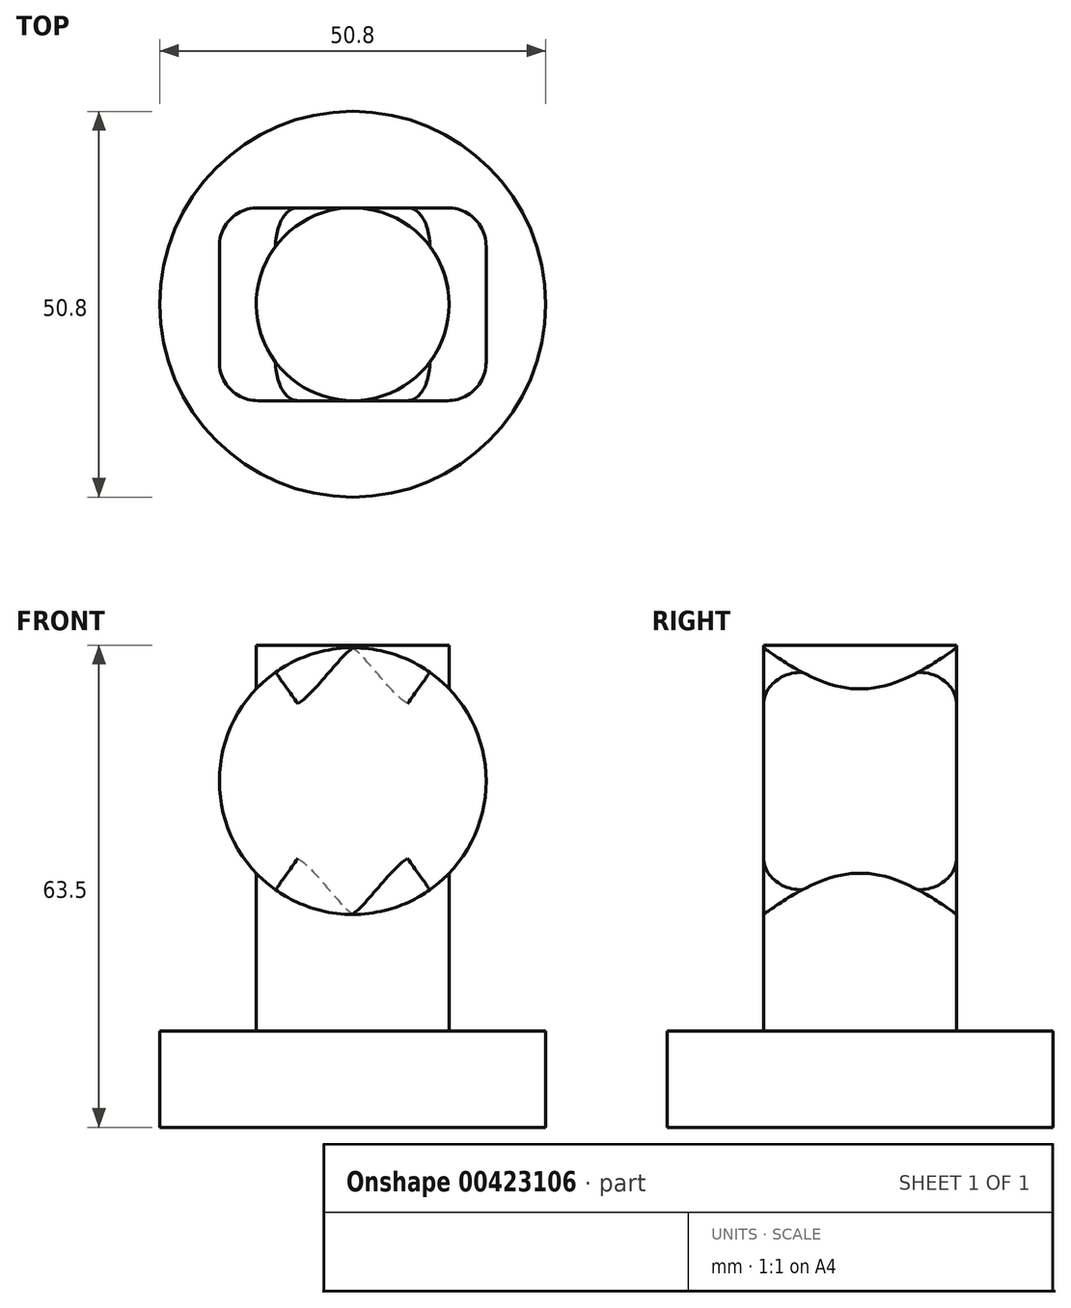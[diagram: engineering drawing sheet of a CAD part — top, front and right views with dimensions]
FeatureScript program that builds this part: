
annotation { "Feature Type Name" : "Feature", "Feature Type Description" : "" }
export const myFeature = defineFeature(function(context is Context, id is Id, definition is map)
    precondition{}
    {
        {
            var Q0;
            Q0=qCreatedBy(makeId("Top.planeOp"),FACE);
            var sketch = newSketch(context, id + "F0", { "sketchPlane" : qUnion([Q0])});
            skCircle(sketch, "E0", {"center": v(0, 0) * mm, "radius": 25.4 * mm});
            skSolve(sketch);
        }
        {
            var Q0;
            Q0=makeQuery(id+"F0.imprint","IMPRINT",FACE,{"disambiguationData":[TD([[makeQuery(id+"F0.imprint","IMPRINT",EDGE,{"derivedFrom":sQuery(id+"F0.wireOp",EDGE,"E0")}),1.0]])]});
            extrude(context, id + "F1", {"entities" : qUnion([Q0]), "depth" : 12.7 * mm});
        }
        {
            var Q0;
            Q0=makeQuery(id+"F1.opExtrude","CAP_FACE",FACE,{"disambiguationData":[OSD([sQuery(id+"F0.wireOp",EDGE,"E0")])],"isStart":false});
            var sketch = newSketch(context, id + "F2", { "sketchPlane" : qUnion([Q0])});
            skCircle(sketch, "E1", {"center": v(0, 0) * mm, "radius": 12.7 * mm});
            skSolve(sketch);
        }
        {
            var Q0;
            Q0=makeQuery(id+"F2.imprint","IMPRINT",FACE,{"disambiguationData":[TD([[makeQuery(id+"F2.imprint","IMPRINT",EDGE,{"derivedFrom":sQuery(id+"F2.wireOp",EDGE,"E1")}),1.0]])]});
            extrude(context, id + "F3", {"entities" : qUnion([Q0]), "operationType" : NewBodyOperationType.ADD, "depth" : 50.8 * mm});
        }
        {
            var Q0;
            Q0=qCreatedBy(makeId("Front.planeOp"),FACE);
            cPlane(context, id + "F4", {"entities" : qUnion([Q0]), "cplaneType" : CPlaneType.OFFSET, "offset" : 12.7 * mm, "width" : 152.4 * mm, "height" : 152.4 * mm});
        }
        {
            var Q0;
            Q0=qCreatedBy(id+"F4.planeOp",FACE);
            var sketch = newSketch(context, id + "F5", { "sketchPlane" : qUnion([Q0])});
            skCircle(sketch, "E2", {"center": v(0, 45.6) * mm, "radius": 17.56 * mm});
            skSolve(sketch);
        }
        {
            var Q0;
            Q0=makeQuery(id+"F5.imprint","IMPRINT",FACE,{"disambiguationData":[TD([[makeQuery(id+"F5.imprint","IMPRINT",EDGE,{"derivedFrom":sQuery(id+"F5.wireOp",EDGE,"E2")}),1.0]])]});
            extrude(context, id + "F6", {"entities" : qUnion([Q0]), "operationType" : NewBodyOperationType.ADD, "oppositeDirection" : true, "depth" : 25.4 * mm});
        }
        {
            var Q0;
            Q0=makeQuery(id+"F6.boolean.opBoolean","SPLIT",EDGE,{"disambiguationData":[OD(0.0)],"derivedFrom":makeQuery(id+"F6.opExtrude","CAP_EDGE",EDGE,{"disambiguationData":[OSD([sQuery(id+"F5.wireOp",EDGE,"E2")])],"isStart":true})});
            var Q1;
            Q1=makeQuery(id+"F6.boolean.opBoolean","SPLIT",EDGE,{"disambiguationData":[OD(1.0)],"derivedFrom":makeQuery(id+"F6.opExtrude","CAP_EDGE",EDGE,{"disambiguationData":[OSD([sQuery(id+"F5.wireOp",EDGE,"E2")])],"isStart":false})});
            fillet(context, id + "F7", {"entities" : qUnion([Q0, Q1]), "radius" : 5.08 * mm, "tangentPropagation" : true, "allowEdgeOverflow" : false});
        }
    });
